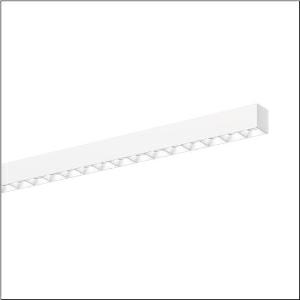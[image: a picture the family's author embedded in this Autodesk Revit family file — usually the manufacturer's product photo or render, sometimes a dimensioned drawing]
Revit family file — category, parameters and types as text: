
# Revit family: silica_r__21_51mx26db35wb_1250
name_source: partatom
category: Lighting Fixtures
units: mm (PartAtom-declared; Revit-internal decimal feet)

## family parameters
Cut with Voids When Loaded = No
Host = Face
Light Source = No
Part Type = Normal
Room Calculation Point = No
Round Connector Dimension = Use Diameter
Shared = No

## types (1)
- --- (1 x LED, 5400 lm, 31.4 W, 3000K)
    Apparent Load = 31 VA
    CIE Flux Codes = 83 98 100 100 100
    Color Rendering = 80
    Color Temperature = 3000K
    Default Elevation = 1800 mm
    Description = Silica® 21, office luminaire, primary light control with darklight reflector, of PMMA, white, CAT 2 (L<= 3000cd/m²), light emission: direct distribution, primary light characteristic: symmetric, installation type: surface-mounted, LED, rated luminous flux: 5.400lm, luminous efficacy: 172lm/W, light colour: 830, colour temperature: 3000K, with terminal, 3+2-pole, max. 2.5mm², mains connection: 220..240V, AC, 50/60Hz, rated input power: 31.4W, luminaire housing, of aluminium, traffic white (RAL 9016), length: 1.504mm, width: 53mm, height: 53mm, protection rating (complete): IP20, insulation class (complete): insulation class I (protective earthing), certification: CE, permissible operating ambient temperature: 0..+35°C, standard: EN 50419, packaging unit: 1 piece
    Height = 0 mm  [stored 0 ft]
    Lamp = 1 x LED
    Lamp Light Flux = 5400 lm
    Lamp Power = 31.4 W
    Lamp count = 1
    Length = 1504 mm
    Luminous efficacy = 172 lm/W
    Manufacturer = Siteco
    ModVariant = No
    Model = 51MX26DB35WB
    Mounting Place = Ceiling
    Mounting Type = Recessed
    Number of Poles = 1
    OnlyDefault = Yes
    Power Factor = 1
    Product Name = Silica® 21
    Product group = office luminaire | ceiling recessed
    ProductGroupID = 401
    Protection Class = Protection class I
    Protection Degree = IP 20
    RLX_Detail_Level = 1
    RLX_Emergency_Light_Flux = 0 lm
    RLX_Emergency_Type = 0
    RLX_Emergency_Type_DB = No
    RlxData = <blob elided: 41973 chars, md5=480db25b>
    Socket = socket
    Standby Power = 0 W
    System Light Flux = 5400 lm
    System Power = 31 W
    Type Comments = factory setting: luminous flux: 100 % | dim-lin: 254 | 360 mA
    Type Image = l_1313597.jpg
    URL = http://relux.com
    VarID = @adj_073525
    Voltage = 0 V
    Weight = 0.00 kg
    Width = 53 mm

note: [stored X ft] marks values corroborated as IEEE doubles in the binary element streams (Revit-internal decimal feet)

## geometry (parser evidence)
native form markers: Blend x4, Sweep x10
no freeform markers — native parametric forms only
